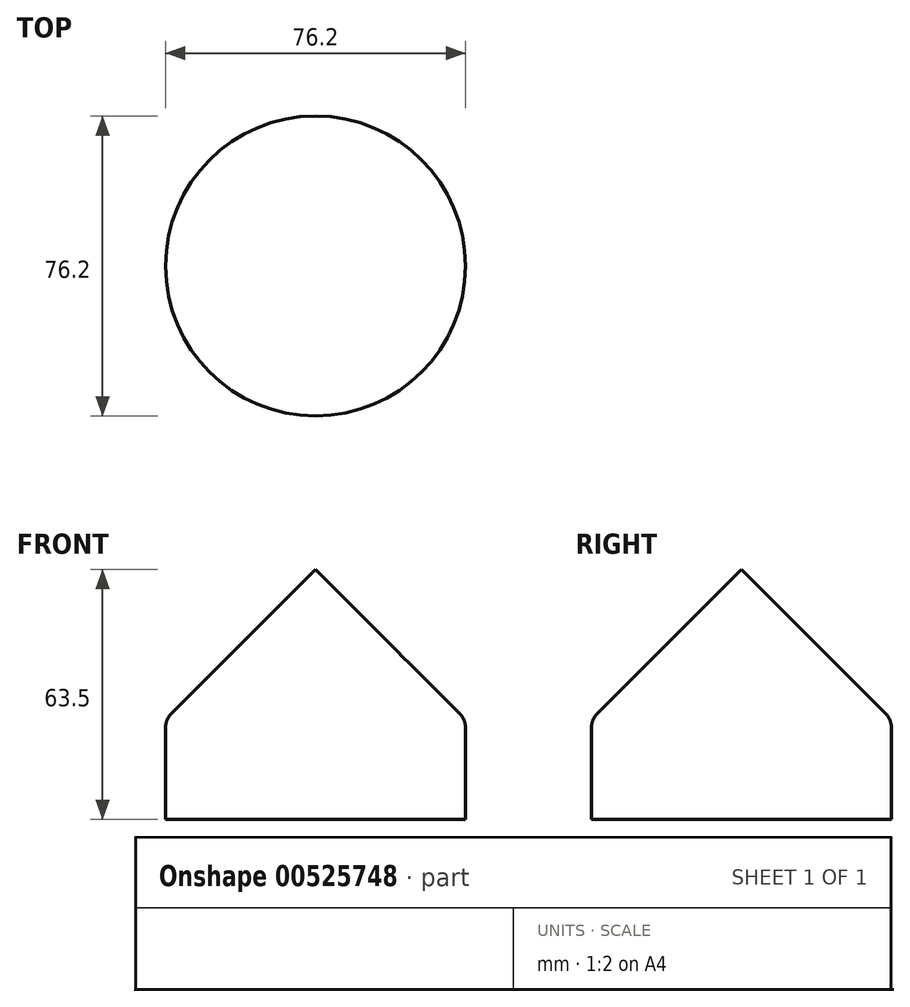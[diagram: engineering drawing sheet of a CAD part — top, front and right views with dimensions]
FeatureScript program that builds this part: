
annotation { "Feature Type Name" : "Feature", "Feature Type Description" : "" }
export const myFeature = defineFeature(function(context is Context, id is Id, definition is map)
    precondition{}
    {
        {
            var Q0;
            Q0=qCreatedBy(makeId("Top.planeOp"),FACE);
            var sketch = newSketch(context, id + "F0", { "sketchPlane" : qUnion([Q0])});
            skCircle(sketch, "E0", {"center": v(0, 0) * mm, "radius": 38.1 * mm});
            skSolve(sketch);
        }
        {
            var Q0;
            Q0=makeQuery(id+"F0.imprint","IMPRINT",FACE,{"disambiguationData":[TD([[makeQuery(id+"F0.imprint","IMPRINT",EDGE,{"derivedFrom":sQuery(id+"F0.wireOp",EDGE,"E0")}),1.0]])]});
            extrude(context, id + "F1", {"entities" : qUnion([Q0]), "depth" : 25.4 * mm, "offsetDistance" : 25.4 * mm});
        }
        {
            var Q0;
            Q0=makeQuery(id+"F1.opExtrude","CAP_FACE",FACE,{"disambiguationData":[OSD([sQuery(id+"F0.wireOp",EDGE,"E0")])],"isStart":false});
            var sketch = newSketch(context, id + "F2", { "sketchPlane" : qUnion([Q0])});
            skCircle(sketch, "E1", {"center": v(0, 0) * mm, "radius": 38.1 * mm});
            skSolve(sketch);
        }
        {
            var Q0;
            Q0 = qSketchRegion(id + "F2", true);
            extrude(context, id + "F3", {"entities" : qUnion([Q0]), "operationType" : NewBodyOperationType.ADD, "depth" : 38.1 * mm, "offsetDistance" : 25.4 * mm, "hasDraft" : true, "draftAngle" : 45 * degree, "draftPullDirection" : true});
        }
        {
            var Q0;
            Q0=makeQuery(id+"F3.boolean.opBoolean","MERGE",EDGE,{"derivedFrom":[makeQuery(id+"F1.opExtrude","CAP_EDGE",EDGE,{"disambiguationData":[OSD([sQuery(id+"F0.wireOp",EDGE,"E0")])],"isStart":false}),makeQuery(id+"F3.opExtrude","CAP_EDGE",EDGE,{"disambiguationData":[OSD([sQuery(id+"F2.wireOp",EDGE,"E1")])],"isStart":true})]});
            fillet(context, id + "F4", {"entities" : qUnion([Q0]), "radius" : 5.08 * mm, "tangentPropagation" : true, "allowEdgeOverflow" : false});
        }
    });
